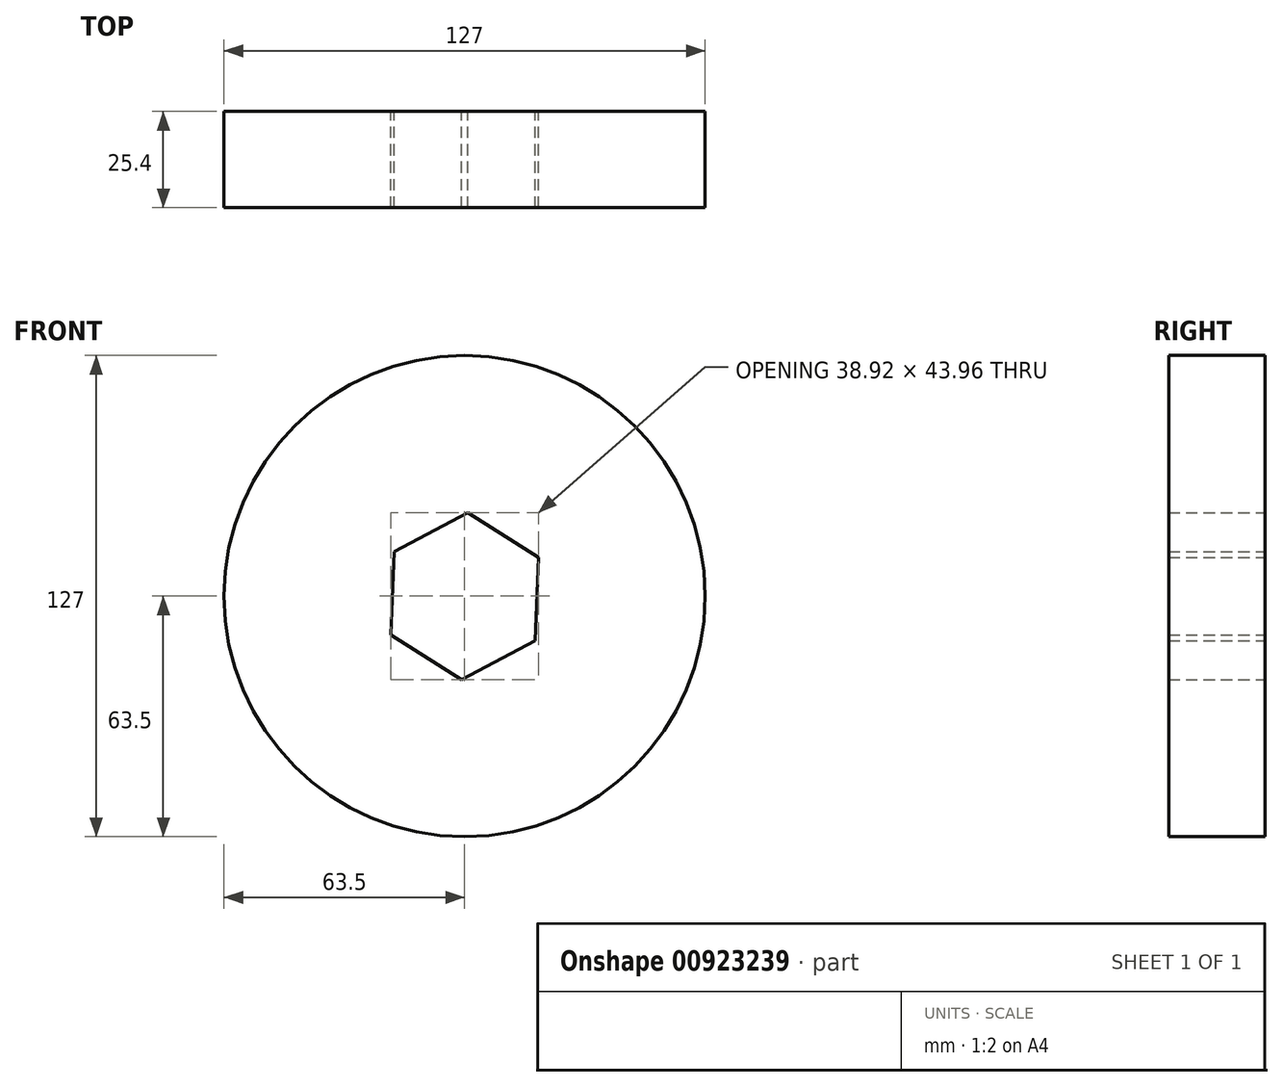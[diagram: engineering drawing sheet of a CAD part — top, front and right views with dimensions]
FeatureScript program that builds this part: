
annotation { "Feature Type Name" : "Feature", "Feature Type Description" : "" }
export const myFeature = defineFeature(function(context is Context, id is Id, definition is map)
    precondition{}
    {
        {
            var Q0;
            Q0=qCreatedBy(makeId("Front.planeOp"),FACE);
            var sketch = newSketch(context, id + "F0", { "sketchPlane" : qUnion([Q0])});
            skCircle(sketch, "E0", {"center": v(0, 0) * mm, "radius": 63.5 * mm});
            skCircle(sketch, "E1.cCircle", {"center": v(0, 0) * mm, "radius": 19.05 * mm, "construction": true});
            skLineSegment(sketch, "E1.0", {"start": v(-18.61, 11.73) * mm, "end": v(0.85, 21.98) * mm});
            skLineSegment(sketch, "E1.1", {"start": v(0.85, 21.98) * mm, "end": v(19.46, 10.25) * mm});
            skLineSegment(sketch, "E1.2", {"start": v(19.46, 10.25) * mm, "end": v(18.61, -11.73) * mm});
            skLineSegment(sketch, "E1.3", {"start": v(18.61, -11.73) * mm, "end": v(-0.85, -21.98) * mm});
            skLineSegment(sketch, "E1.4", {"start": v(-0.85, -21.98) * mm, "end": v(-19.46, -10.25) * mm});
            skLineSegment(sketch, "E1.5", {"start": v(-19.46, -10.25) * mm, "end": v(-18.61, 11.73) * mm});
            skPoint(sketch, "E1.0.midPoint", {"position": v(-8.88, 16.85) * mm});
            skSolve(sketch);
        }
        {
            var Q0;
            Q0=makeQuery(id+"F0.imprint","IMPRINT",FACE,{"disambiguationData":[TD([[makeQuery(id+"F0.imprint","IMPRINT",EDGE,{"derivedFrom":sQuery(id+"F0.wireOp",EDGE,"E0")}),1.0]])]});
            extrude(context, id + "F1", {"entities" : qUnion([Q0]), "depth" : 25.4 * mm, "offsetDistance" : 25.4 * mm});
        }
    });
